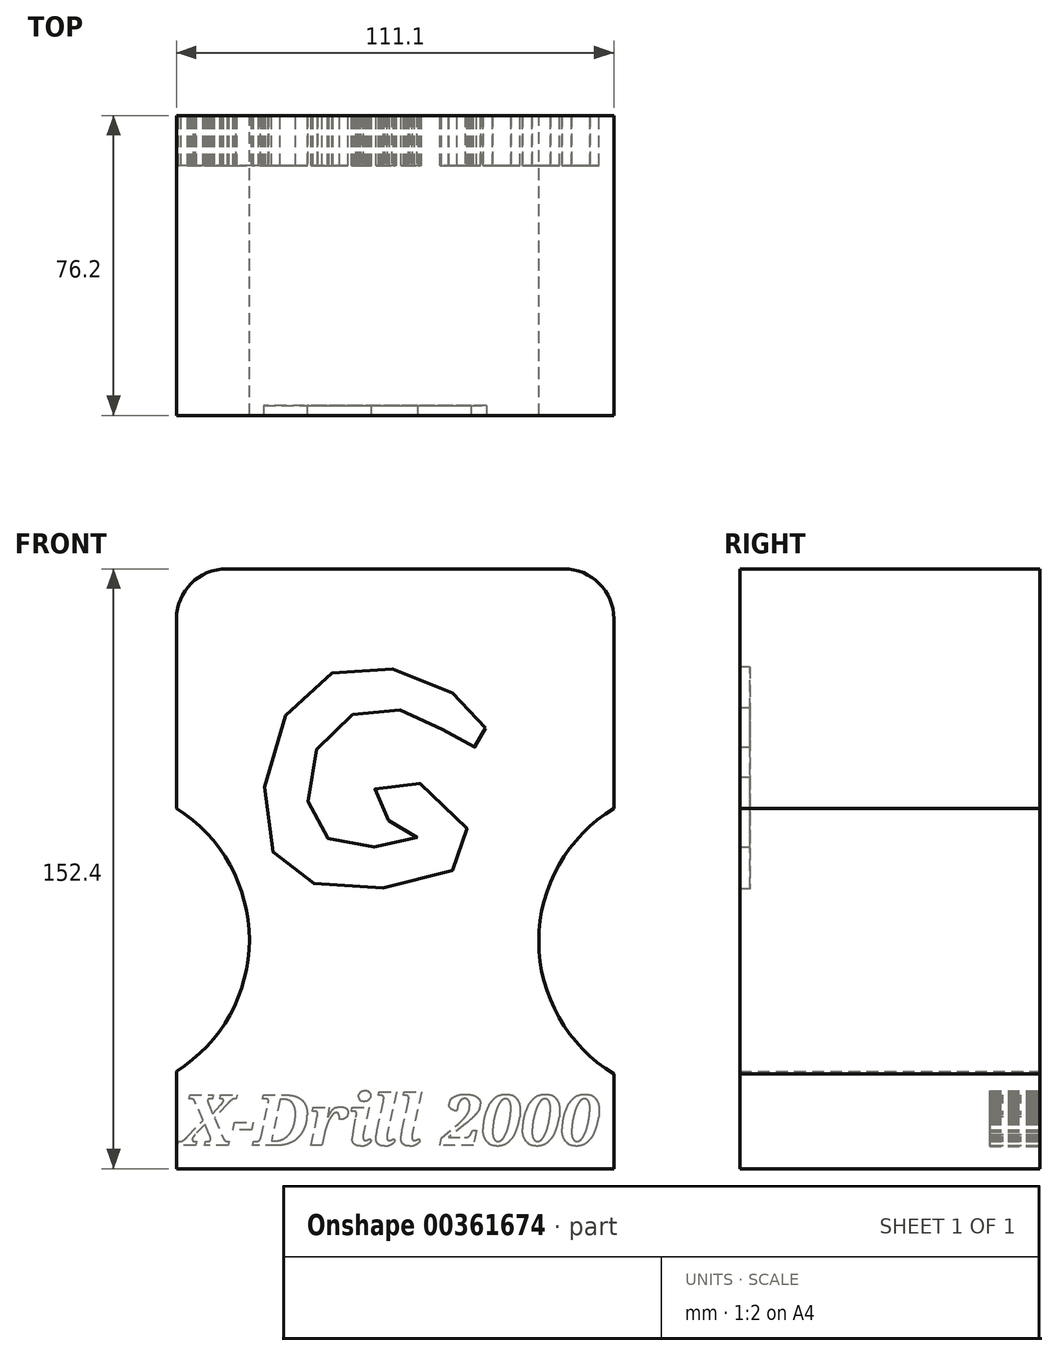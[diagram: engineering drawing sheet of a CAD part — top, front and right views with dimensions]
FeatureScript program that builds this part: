
annotation { "Feature Type Name" : "Feature", "Feature Type Description" : "" }
export const myFeature = defineFeature(function(context is Context, id is Id, definition is map)
    precondition{}
    {
        {
            var Q0;
            Q0=qCreatedBy(makeId("Front.planeOp"),FACE);
            var sketch = newSketch(context, id + "F0", { "sketchPlane" : qUnion([Q0])});
            skLineSegment(sketch, "E0.bottom", {"start": v(-52.58, 60.88) * mm, "end": v(33.12, 60.88) * mm});
            skLineSegment(sketch, "E0.top", {"start": v(-65.28, -91.52) * mm, "end": v(45.82, -91.52) * mm});
            skLineSegment(sketch, "E0.left", {"start": v(-65.28, 48.18) * mm, "end": v(-65.28, -91.52) * mm});
            skLineSegment(sketch, "E0.right", {"start": v(45.82, 48.18) * mm, "end": v(45.82, -91.52) * mm});
            skPoint(sketch, "E1.visualSharp", {"position": v(-65.28, 60.88) * mm});
            skArc(sketch, "E1.filletArc", {"start": v(-52.58, 60.88) * mm, "mid": v(-61.56, 57.16) * mm, "end": v(-65.28, 48.18) * mm});
            skPoint(sketch, "E2.visualSharp", {"position": v(45.82, 60.88) * mm});
            skArc(sketch, "E2.filletArc", {"start": v(45.82, 48.18) * mm, "mid": v(42.1, 57.16) * mm, "end": v(33.12, 60.88) * mm});
            skArc(sketch, "E3", {"start": v(-65.28, -66.76) * mm, "mid": v(-46.78, -33.38) * mm, "end": v(-65.28, 0) * mm});
            skArc(sketch, "E4", {"start": v(45.82, 0) * mm, "mid": v(26.77, -33.72) * mm, "end": v(45.82, -67.44) * mm});
            skSolve(sketch);
        }
        {
            var Q0;
            Q0=makeQuery(id+"F0.imprint","IMPRINT",FACE,{"disambiguationData":[TD([[makeQuery(id+"F0.imprint","IMPRINT",EDGE,{"derivedFrom":sQuery(id+"F0.wireOp",EDGE,"E0.bottom")}),-1.0]])]});
            extrude(context, id + "F1", {"entities" : qUnion([Q0]), "depth" : 76.2 * mm});
        }
        {
            var Q0;
            Q0=makeQuery(id+"F1.opExtrude","CAP_FACE",FACE,{"disambiguationData":[OSD([sQuery(id+"F0.wireOp",EDGE,"E0.bottom"),sQuery(id+"F0.wireOp",EDGE,"E0.top"),sQuery(id+"F0.wireOp",EDGE,"E0.left"),sQuery(id+"F0.wireOp",EDGE,"E0.right"),sQuery(id+"F0.wireOp",EDGE,"E1.filletArc"),sQuery(id+"F0.wireOp",EDGE,"E2.filletArc"),sQuery(id+"F0.wireOp",EDGE,"E3"),sQuery(id+"F0.wireOp",EDGE,"E4")])],"isStart":false});
            var sketch = newSketch(context, id + "F2", { "sketchPlane" : qUnion([Q0])});
            skFitSpline(sketch, "E5", {"points": [v(13.28, 20.44) * mm, v(-6.47, 34.4) * mm, v(-34.06, 28.62) * mm, v(-41.56, -9.2) * mm, v(-20.44, -20.43) * mm, v(9.54, -9.87) * mm, v(-9.54, 7.84) * mm, v(-15.33, 0) * mm, v(-4.09, -6.8) * mm, v(-17.37, -9.87) * mm, v(-30.32, -3.74) * mm, v(-28.95, 16.35) * mm, v(-12.6, 25.55) * mm, v(3.75, 19.08) * mm, v(11.58, 15.67) * mm, v(13.28, 20.44) * mm]});
            skSolve(sketch);
        }
        {
            var Q0;
            Q0=makeQuery(id+"F2.imprint","IMPRINT",FACE,{"disambiguationData":[TD([[makeQuery(id+"F2.imprint","IMPRINT",EDGE,{"derivedFrom":sQuery(id+"F2.wireOp",EDGE,"E5")}),1.0]])]});
            extrude(context, id + "F3", {"entities" : qUnion([Q0]), "operationType" : NewBodyOperationType.REMOVE, "oppositeDirection" : true, "depth" : 2.54 * mm});
        }
        {
            var Q0;
            Q0=makeQuery(id+"F0.imprint","IMPRINT",FACE,{"disambiguationData":[TD([[makeQuery(id+"F0.imprint","IMPRINT",EDGE,{"derivedFrom":sQuery(id+"F0.wireOp",EDGE,"E0.bottom")}),-1.0]])]});
            var sketch = newSketch(context, id + "F4", { "sketchPlane" : qUnion([Q0])});
            skText(sketch, "E6", { "text": "X-Drill 2000", "fontName": "NotoSerif-BoldItalic.ttf"});
            const initialGuessF4  = {"E6": [-0.0642, -0.0856, 1, 0, 0.01292]};
            skSetInitialGuess(sketch, initialGuessF4);
            skSolve(sketch);
        }
        {
            var Q0;
            Q0 = qSketchRegion(id + "F4", true);
            extrude(context, id + "F5", {"entities" : qUnion([Q0]), "operationType" : NewBodyOperationType.REMOVE, "depth" : 12.7 * mm});
        }
    });
